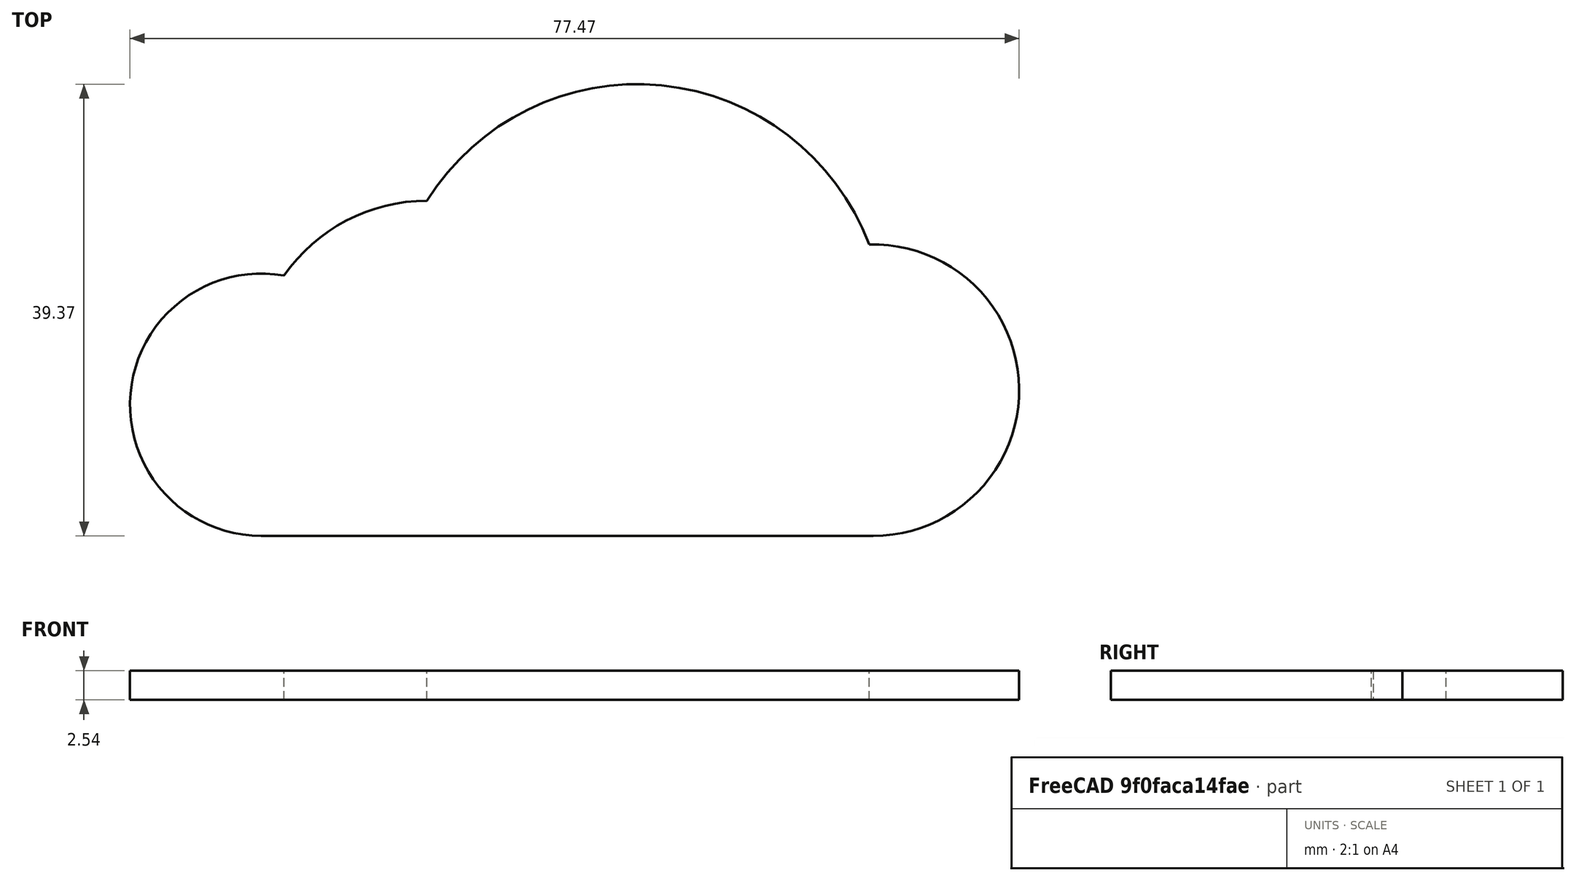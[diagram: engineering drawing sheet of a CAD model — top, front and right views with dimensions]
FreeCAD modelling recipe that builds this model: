
FCSTD DOCUMENT  (FreeCAD 0.16R6712 (Git))
Label: steam_badge3
License: All rights reserved
LicenseURL: http://en.wikipedia.org/wiki/All_rights_reserved
objects: Sketcher::SketchObject×2, PartDesign::Pad×1
note: 4 computed .brp shape members not serialized (recipe doc carries the construction recipe); baked Part::Feature solids carry a one-line shape summary decoded from their .brp

FEATURE [Sketcher::SketchObject] Sketch
  sketch-geometry (11):
    g0: LineSegment [constr] StartX=0 StartY=0 StartZ=0 EndX=28.702 EndY=0 EndZ=0
    g1: LineSegment [constr] StartX=28.702 StartY=0 StartZ=0 EndX=28.702 EndY=38.1 EndZ=0
    g2: ArcOfCircle CenterX=28.702 CenterY=49.53 CenterZ=0 NormalX=0 NormalY=0 NormalZ=1 Radius=11.43 StartAngle=1.39691 EndAngle=4.71239
    g3: LineSegment StartX=28.702 StartY=38.1 StartZ=0 EndX=82.042 EndY=38.1 EndZ=0
    g4: ArcOfCircle CenterX=82.042 CenterY=50.8 CenterZ=0 NormalX=0 NormalY=0 NormalZ=1 Radius=12.7 StartAngle=4.71239 EndAngle=7.88323
    g5: ArcOfCircle CenterX=43.18 CenterY=52.07 CenterZ=0 NormalX=0 NormalY=0 NormalZ=1 Radius=15.24 StartAngle=1.57265 EndAngle=2.53262
    g6: LineSegment [constr] StartX=43.18 StartY=52.07 StartZ=0 EndX=61.468 EndY=52.07 EndZ=0
    g7: LineSegment [constr] StartX=61.468 StartY=52.07 StartZ=0 EndX=61.468 EndY=55.88 EndZ=0
    g8: ArcOfCircle CenterX=61.468 CenterY=55.88 CenterZ=0 NormalX=0 NormalY=0 NormalZ=1 Radius=21.59 StartAngle=0.360444 EndAngle=2.58369
    g9: LineSegment [constr] StartX=28.702 StartY=49.53 StartZ=0 EndX=43.18 EndY=49.53 EndZ=0
    g10: LineSegment [constr] StartX=43.18 StartY=49.53 StartZ=0 EndX=43.18 EndY=52.07 EndZ=0
  constraints (34):
    c: Coincident(g-1,g0)
    c: PointOnObject(g0,g-1)
    c: Vertical(g1)
    c: DistanceX(g0,g0) = 28.702
    c: DistanceY(g1,g2) = 49.53
    c: Radius(g2) = 11.43
    c: Horizontal(g3)
    c: DistanceX(g3,g3) = 53.34
    c: DistanceX(g2,g3) = 0
    c: DistanceX(g4,g3) = 0
    c: Radius(g4) = 12.7
    c: Coincident(g0,g1)
    c: Radius(g5) = 15.24
    c: Horizontal(g6)
    c: Vertical(g7)
    c: DistanceX(g6,g6) = 18.288
    c: Coincident(g6,g7)
    c: Radius(g8) = 21.59
    c: Horizontal(g9)
    c: Coincident(g2,g9)
    c: DistanceX(g9,g9) = 14.478
    c: Vertical(g10)
    c: Coincident(g9,g10)
    c: DistanceY(g10,g10) = 2.54
    c: Coincident(g2,g5)
    c: Coincident(g2,g1)
    c: Coincident(g1,g3)
    c: Coincident(g3,g4)
    c: Coincident(g10,g5)
    c: Coincident(g6,g5)
    c: DistanceY(g7,g7) = 3.81
    c: Coincident(g7,g8)
    c: Coincident(g8,g5)
    c: Coincident(g4,g8)
FEATURE [PartDesign::Pad] Pad
  Length = 2.54
  Length2 = 100
  Sketch = -> Sketch
  Type = 0
FEATURE [Sketcher::SketchObject] Sketch001
  sketch-geometry (19):
    g0: LineSegment [constr] StartX=0 StartY=0 StartZ=0 EndX=28.702 EndY=0 EndZ=0
    g1: LineSegment [constr] StartX=28.702 StartY=0 StartZ=0 EndX=28.702 EndY=38.1 EndZ=0
    g2: ArcOfCircle CenterX=28.702 CenterY=49.53 CenterZ=0 NormalX=0 NormalY=0 NormalZ=1 Radius=11.43 StartAngle=1.39691 EndAngle=4.71239
    g3: LineSegment StartX=28.702 StartY=38.1 StartZ=0 EndX=82.042 EndY=38.1 EndZ=0
    g4: ArcOfCircle CenterX=82.042 CenterY=50.8 CenterZ=0 NormalX=0 NormalY=0 NormalZ=1 Radius=12.7 StartAngle=4.71239 EndAngle=7.88323
    g5: ArcOfCircle CenterX=43.18 CenterY=52.07 CenterZ=0 NormalX=0 NormalY=0 NormalZ=1 Radius=15.24 StartAngle=1.57265 EndAngle=2.53262
    g6: LineSegment [constr] StartX=43.18 StartY=52.07 StartZ=0 EndX=61.468 EndY=52.07 EndZ=0
    g7: LineSegment [constr] StartX=61.468 StartY=52.07 StartZ=0 EndX=61.468 EndY=55.88 EndZ=0
    g8: ArcOfCircle CenterX=61.468 CenterY=55.88 CenterZ=0 NormalX=0 NormalY=0 NormalZ=1 Radius=21.59 StartAngle=0.360444 EndAngle=2.58369
    g9: LineSegment [constr] StartX=28.702 StartY=49.53 StartZ=0 EndX=43.18 EndY=49.53 EndZ=0
    g10: LineSegment [constr] StartX=43.18 StartY=49.53 StartZ=0 EndX=43.18 EndY=52.07 EndZ=0
    g11: ArcOfCircle CenterX=28.702 CenterY=49.53 CenterZ=0 NormalX=0 NormalY=0 NormalZ=1 Radius=12.7 StartAngle=1.46002 EndAngle=4.71239
    g12: ArcOfCircle CenterX=43.18 CenterY=52.07 CenterZ=0 NormalX=0 NormalY=0 NormalZ=1 Radius=16.51 StartAngle=1.61505 EndAngle=2.48469
    g13: ArcOfCircle CenterX=61.468 CenterY=55.88 CenterZ=0 NormalX=0 NormalY=0 NormalZ=1 Radius=22.86 StartAngle=0.399017 EndAngle=2.55341
    g14: ArcOfCircle CenterX=82.042 CenterY=50.8 CenterZ=0 NormalX=0 NormalY=0 NormalZ=1 Radius=13.97 StartAngle=4.26334 EndAngle=4.28269
    g15: ArcOfCircle CenterX=61.468 CenterY=55.88 CenterZ=0 NormalX=0 NormalY=0 NormalZ=1 Radius=22.86 StartAngle=5.39206 EndAngle=5.40003
    g16: LineSegment StartX=28.448 StartY=36.8309 StartZ=0 EndX=81.8875 EndY=36.8309 EndZ=0
    g17: ArcOfCircle CenterX=28.702 CenterY=49.53 CenterZ=0 NormalX=0 NormalY=0 NormalZ=1 Radius=12.7 StartAngle=5.16342 EndAngle=5.17142
    g18: ArcOfCircle CenterX=82.042 CenterY=50.8 CenterZ=0 NormalX=0 NormalY=0 NormalZ=1 Radius=13.97 StartAngle=4.70133 EndAngle=7.81889
  constraints (55):
    c: Coincident(g-1,g0)
    c: PointOnObject(g0,g-1)
    c: Vertical(g1)
    c: DistanceX(g0,g0) = 28.702
    c: DistanceY(g1,g2) = 49.53
    c: Radius(g2) = 11.43
    c: Horizontal(g3)
    c: DistanceX(g3,g3) = 53.34
    c: DistanceX(g2,g3) = 0
    c: DistanceX(g4,g3) = 0
    c: Radius(g4) = 12.7
    c: Coincident(g0,g1)
    c: Radius(g5) = 15.24
    c: Horizontal(g6)
    c: Vertical(g7)
    c: DistanceX(g6,g6) = 18.288
    c: Coincident(g6,g7)
    c: Radius(g8) = 21.59
    c: Horizontal(g9)
    c: Coincident(g2,g9)
    c: DistanceX(g9,g9) = 14.478
    c: Vertical(g10)
    c: Coincident(g9,g10)
    c: DistanceY(g10,g10) = 2.54
    c: Coincident(g2,g5)
    c: Coincident(g2,g1)
    c: Coincident(g1,g3)
    c: Coincident(g3,g4)
    c: Coincident(g10,g5)
    c: Coincident(g6,g5)
    c: DistanceY(g7,g7) = 3.81
    c: Coincident(g7,g8)
    c: Coincident(g8,g5)
    c: Coincident(g4,g8)
    c: Radius(g11) = 12.7
    c: Coincident(g2,g11)
    c: Radius(g12) = 16.51
    c: Radius(g13) = 22.86
    c: Radius(g14) = 13.97
    c: Coincident(g4,g14)
    c: Coincident(g7,g13)
    c: Coincident(g5,g12)
    c: Equal(g13,g15)
    c: Coincident(g13,g15)
    c: Horizontal(g16)
    c: Equal(g11,g17)
    c: PointOnObject(g11,g1)
    c: Coincident(g11,g17)
    c: Equal(g14,g18)
    c: Coincident(g14,g18)
    c: Coincident(g11,g12)
    c: Coincident(g12,g13)
    c: Coincident(g13,g18)
    c: Coincident(g16,g18)
    c: Coincident(g16,g11)
